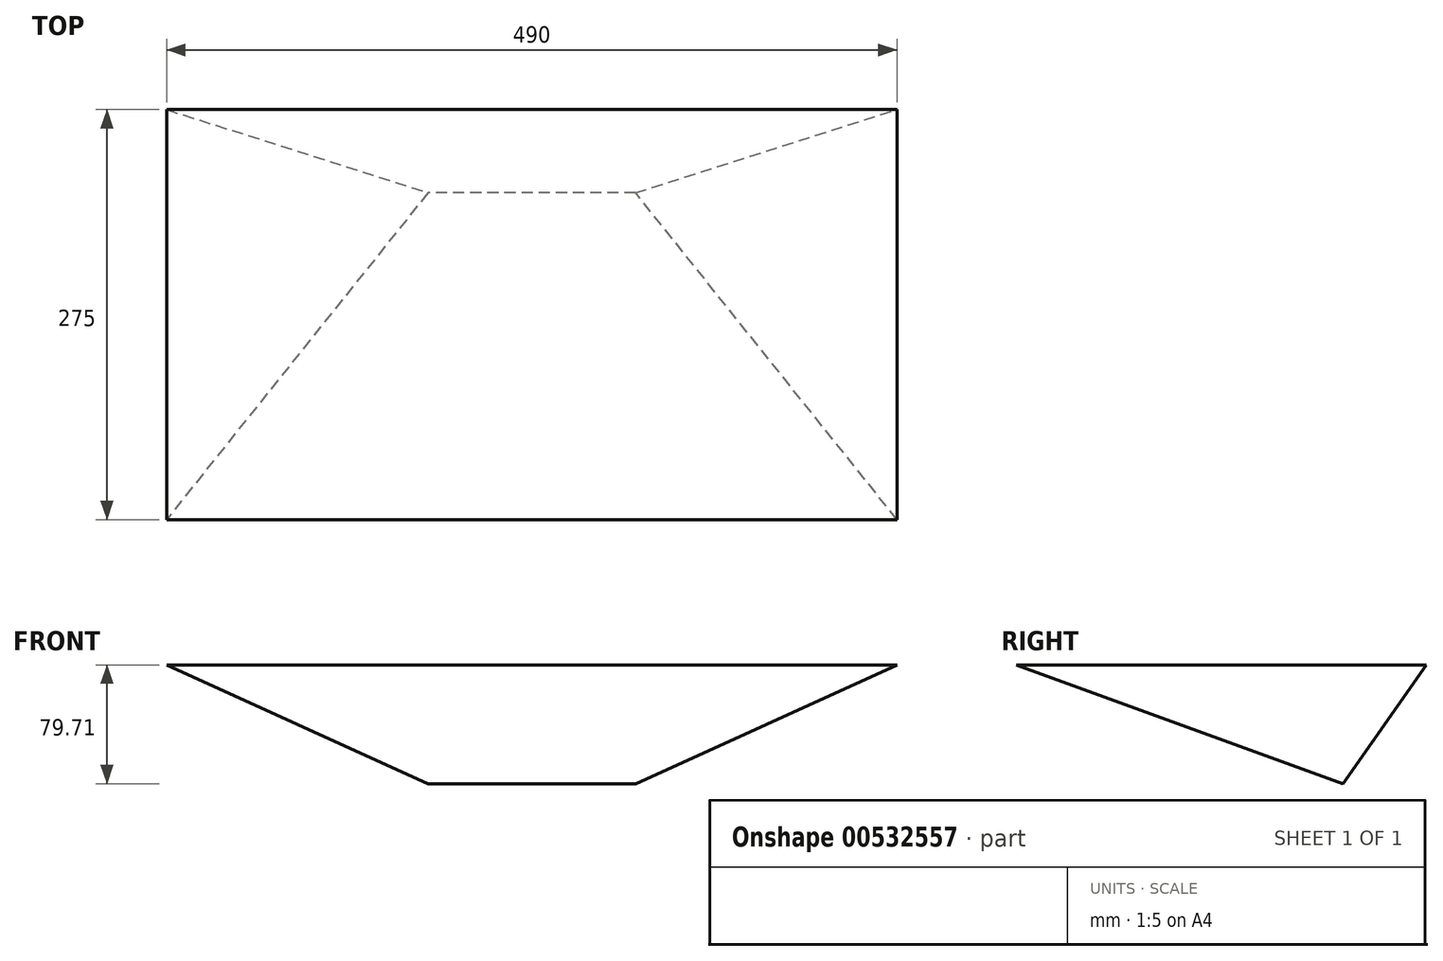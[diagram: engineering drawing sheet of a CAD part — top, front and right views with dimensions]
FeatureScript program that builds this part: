
annotation { "Feature Type Name" : "Feature", "Feature Type Description" : "" }
export const myFeature = defineFeature(function(context is Context, id is Id, definition is map)
    precondition{}
    {
        {
            var Q0;
            Q0=qCreatedBy(makeId("Right.planeOp"),FACE);
            var sketch = newSketch(context, id + "F0", { "sketchPlane" : qUnion([Q0])});
            skLineSegment(sketch, "E0.bottom", {"start": v(-137.5, 50) * mm, "end": v(137.5, 50) * mm});
            skLineSegment(sketch, "E0.top", {"start": v(-137.5, -50) * mm, "end": v(137.5, -50) * mm});
            skLineSegment(sketch, "E0.left", {"start": v(-137.5, 50) * mm, "end": v(-137.5, -50) * mm});
            skLineSegment(sketch, "E0.right", {"start": v(137.5, 50) * mm, "end": v(137.5, -50) * mm});
            skPoint(sketch, "E0.middle", {"position": v(0, 0) * mm});
            skSolve(sketch);
        }
        {
            var Q0;
            Q0 = qSketchRegion(id + "F0", true);
            extrude(context, id + "F1", {"entities" : qUnion([Q0]), "depth" : 490 * mm, "offsetDistance" : 25 * mm});
        }
        {
            var Q0;
            Q0=makeQuery(id+"F1.opExtrude","SWEPT_FACE",FACE,{"disambiguationData":[OSD([sQuery(id+"F0.wireOp",EDGE,"E0.left")])]});
            var sketch = newSketch(context, id + "F2", { "sketchPlane" : qUnion([Q0])});
            skLineSegment(sketch, "E1.top", {"start": v(0, -50) * mm, "end": v(490, -50) * mm});
            skLineSegment(sketch, "E1.left", {"start": v(0, 50) * mm, "end": v(0, -50) * mm});
            skLineSegment(sketch, "E1.right", {"start": v(490, 50) * mm, "end": v(490, -50) * mm});
            skPoint(sketch, "E1.middle", {"position": v(245, 0) * mm});
            skPoint(sketch, "E1.middle.positionSnap0", {"position": v(245, 50) * mm});
            skPoint(sketch, "E1.centerSnap0", {"position": v(245, 50) * mm});
            skLineSegment(sketch, "E2", {"start": v(0, 50) * mm, "end": v(220, -50) * mm});
            skLineSegment(sketch, "E3", {"start": v(270, -50) * mm, "end": v(490, 50) * mm});
            skPoint(sketch, "E4.bottom.end.orphan", {"position": v(270, 50) * mm});
            skPoint(sketch, "E5.orphan", {"position": v(220, 50) * mm});
            skSolve(sketch);
        }
        {
            var Q0;
            Q0 = qSketchRegion(id + "F2", true);
            extrude(context, id + "F3", {"entities" : qUnion([Q0]), "operationType" : NewBodyOperationType.REMOVE, "endBound" : BoundingType.THROUGH_ALL, "oppositeDirection" : true, "depth" : 25 * mm, "offsetDistance" : 25 * mm});
        }
        {
            var Q0;
            Q0=qCreatedBy(makeId("Right.planeOp"),FACE);
            var sketch = newSketch(context, id + "F4", { "sketchPlane" : qUnion([Q0])});
            skPoint(sketch, "E6.middle", {"position": v(0, 0) * mm});
            skLineSegment(sketch, "E7", {"start": v(81.69, -29.7) * mm, "end": v(-137.5, 50) * mm});
            skPoint(sketch, "E6.top.start.orphan", {"position": v(-137.5, -50) * mm});
            skLineSegment(sketch, "E8.bottom", {"start": v(-137.5, -50) * mm, "end": v(137.5, -50) * mm});
            skLineSegment(sketch, "E8.left", {"start": v(-137.5, -50) * mm, "end": v(-137.5, 50) * mm});
            skLineSegment(sketch, "E9", {"start": v(137.5, -50) * mm, "end": v(137.5, 50) * mm});
            skLineSegment(sketch, "E10", {"start": v(137.5, 50) * mm, "end": v(81.69, -29.7) * mm});
            skSolve(sketch);
        }
        {
            var Q0;
            Q0 = qSketchRegion(id + "F4", true);
            extrude(context, id + "F5", {"entities" : qUnion([Q0]), "operationType" : NewBodyOperationType.REMOVE, "endBound" : BoundingType.THROUGH_ALL, "depth" : 25 * mm, "offsetDistance" : 25 * mm});
        }
    });
